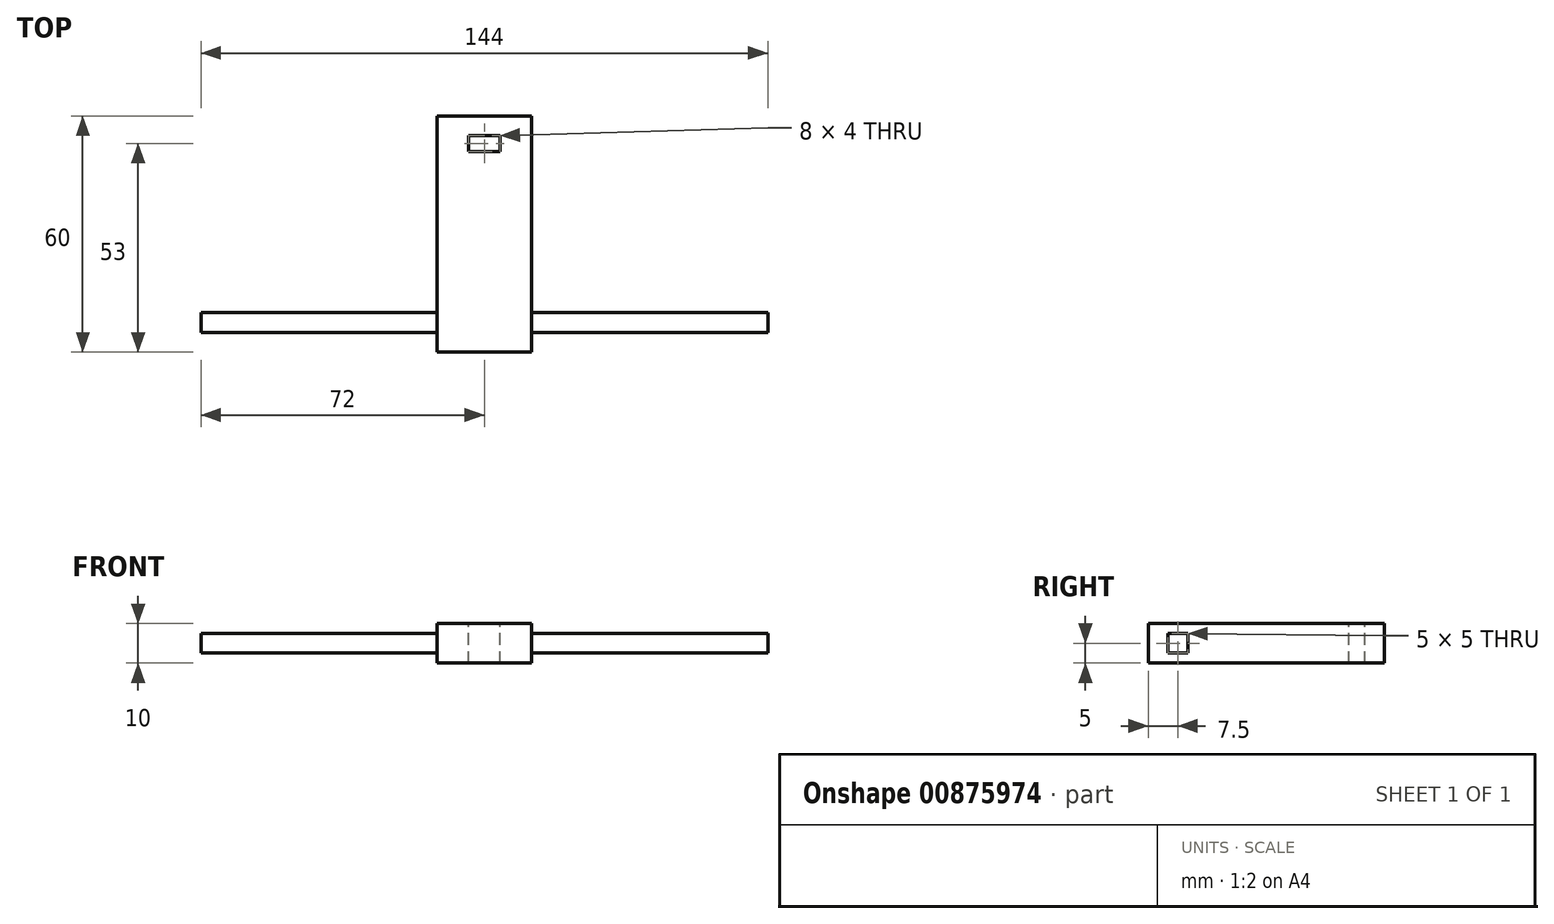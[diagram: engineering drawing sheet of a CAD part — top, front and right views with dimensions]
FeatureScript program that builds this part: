
annotation { "Feature Type Name" : "Feature", "Feature Type Description" : "" }
export const myFeature = defineFeature(function(context is Context, id is Id, definition is map)
    precondition{}
    {
        {
            var Q0;
            Q0=qCreatedBy(makeId("Top.planeOp"),FACE);
            var sketch = newSketch(context, id + "F0", { "sketchPlane" : qUnion([Q0])});
            skLineSegment(sketch, "E0.bottom", {"start": v(12, -30) * mm, "end": v(-12, -30) * mm});
            skLineSegment(sketch, "E0.top", {"start": v(12, 30) * mm, "end": v(-12, 30) * mm});
            skLineSegment(sketch, "E0.left", {"start": v(12, -30) * mm, "end": v(12, 30) * mm});
            skLineSegment(sketch, "E0.right", {"start": v(-12, -30) * mm, "end": v(-12, 30) * mm});
            skPoint(sketch, "E0.middle", {"position": v(0, 0) * mm});
            skSolve(sketch);
        }
        {
            var Q0;
            Q0 = qSketchRegion(id + "F0", true);
            extrude(context, id + "F1", {"entities" : qUnion([Q0]), "depth" : 10 * mm, "offsetDistance" : 25 * mm});
        }
        {
            var Q0;
            Q0=makeQuery(id+"F1.opExtrude","CAP_FACE",FACE,{"disambiguationData":[OSD([sQuery(id+"F0.wireOp",EDGE,"E0.bottom"),sQuery(id+"F0.wireOp",EDGE,"E0.top"),sQuery(id+"F0.wireOp",EDGE,"E0.left"),sQuery(id+"F0.wireOp",EDGE,"E0.right")])],"isStart":false});
            var sketch = newSketch(context, id + "F2", { "sketchPlane" : qUnion([Q0])});
            skLineSegment(sketch, "E1.bottom", {"start": v(4, 21) * mm, "end": v(-4, 21) * mm});
            skLineSegment(sketch, "E1.top", {"start": v(4, 25) * mm, "end": v(-4, 25) * mm});
            skLineSegment(sketch, "E1.left", {"start": v(4, 21) * mm, "end": v(4, 25) * mm});
            skLineSegment(sketch, "E1.right", {"start": v(-4, 21) * mm, "end": v(-4, 25) * mm});
            skPoint(sketch, "E1.middle", {"position": v(0, 23) * mm});
            skPoint(sketch, "E1.middle.positionSnap0", {"position": v(0, 30) * mm});
            skPoint(sketch, "E1.centerSnap0", {"position": v(0, 30) * mm});
            skSolve(sketch);
        }
        {
            var Q0;
            Q0 = qSketchRegion(id + "F2", true);
            extrude(context, id + "F3", {"entities" : qUnion([Q0]), "operationType" : NewBodyOperationType.REMOVE, "oppositeDirection" : true, "depth" : 25 * mm, "offsetDistance" : 25 * mm});
        }
        {
            var Q0;
            Q0=makeQuery(id+"F1.opExtrude","SWEPT_FACE",FACE,{"disambiguationData":[OSD([sQuery(id+"F0.wireOp",EDGE,"E0.left")])]});
            var sketch = newSketch(context, id + "F4", { "sketchPlane" : qUnion([Q0])});
            skLineSegment(sketch, "E2.bottom", {"start": v(-20, 2.5) * mm, "end": v(-25, 2.5) * mm});
            skLineSegment(sketch, "E2.top", {"start": v(-20, 7.5) * mm, "end": v(-25, 7.5) * mm});
            skLineSegment(sketch, "E2.left", {"start": v(-20, 2.5) * mm, "end": v(-20, 7.5) * mm});
            skLineSegment(sketch, "E2.right", {"start": v(-25, 2.5) * mm, "end": v(-25, 7.5) * mm});
            skPoint(sketch, "E2.middle", {"position": v(-22.5, 5) * mm});
            skPoint(sketch, "E2.middle.positionSnap0", {"position": v(-30, 5) * mm});
            skPoint(sketch, "E2.centerSnap0", {"position": v(-30, 5) * mm});
            skSolve(sketch);
        }
        {
            var Q0;
            Q0 = qSketchRegion(id + "F4", true);
            extrude(context, id + "F5", {"entities" : qUnion([Q0]), "operationType" : NewBodyOperationType.ADD, "depth" : 60 * mm, "offsetDistance" : 25 * mm});
        }
        {
            var Q0;
            Q0=makeQuery(id+"F1.opExtrude","SWEPT_FACE",FACE,{"disambiguationData":[OSD([sQuery(id+"F0.wireOp",EDGE,"E0.right")])]});
            var sketch = newSketch(context, id + "F6", { "sketchPlane" : qUnion([Q0])});
            skLineSegment(sketch, "E3.bottom", {"start": v(25, 2.5) * mm, "end": v(20, 2.5) * mm});
            skLineSegment(sketch, "E3.top", {"start": v(25, 7.5) * mm, "end": v(20, 7.5) * mm});
            skLineSegment(sketch, "E3.left", {"start": v(25, 2.5) * mm, "end": v(25, 7.5) * mm});
            skLineSegment(sketch, "E3.right", {"start": v(20, 2.5) * mm, "end": v(20, 7.5) * mm});
            skPoint(sketch, "E3.middle", {"position": v(22.5, 5) * mm});
            skPoint(sketch, "E3.middle.positionSnap0", {"position": v(30, 5) * mm});
            skPoint(sketch, "E3.centerSnap0", {"position": v(30, 5) * mm});
            skSolve(sketch);
        }
        {
            var Q0;
            Q0 = qSketchRegion(id + "F6", true);
            extrude(context, id + "F7", {"entities" : qUnion([Q0]), "operationType" : NewBodyOperationType.ADD, "depth" : 60 * mm, "offsetDistance" : 25 * mm});
        }
    });
